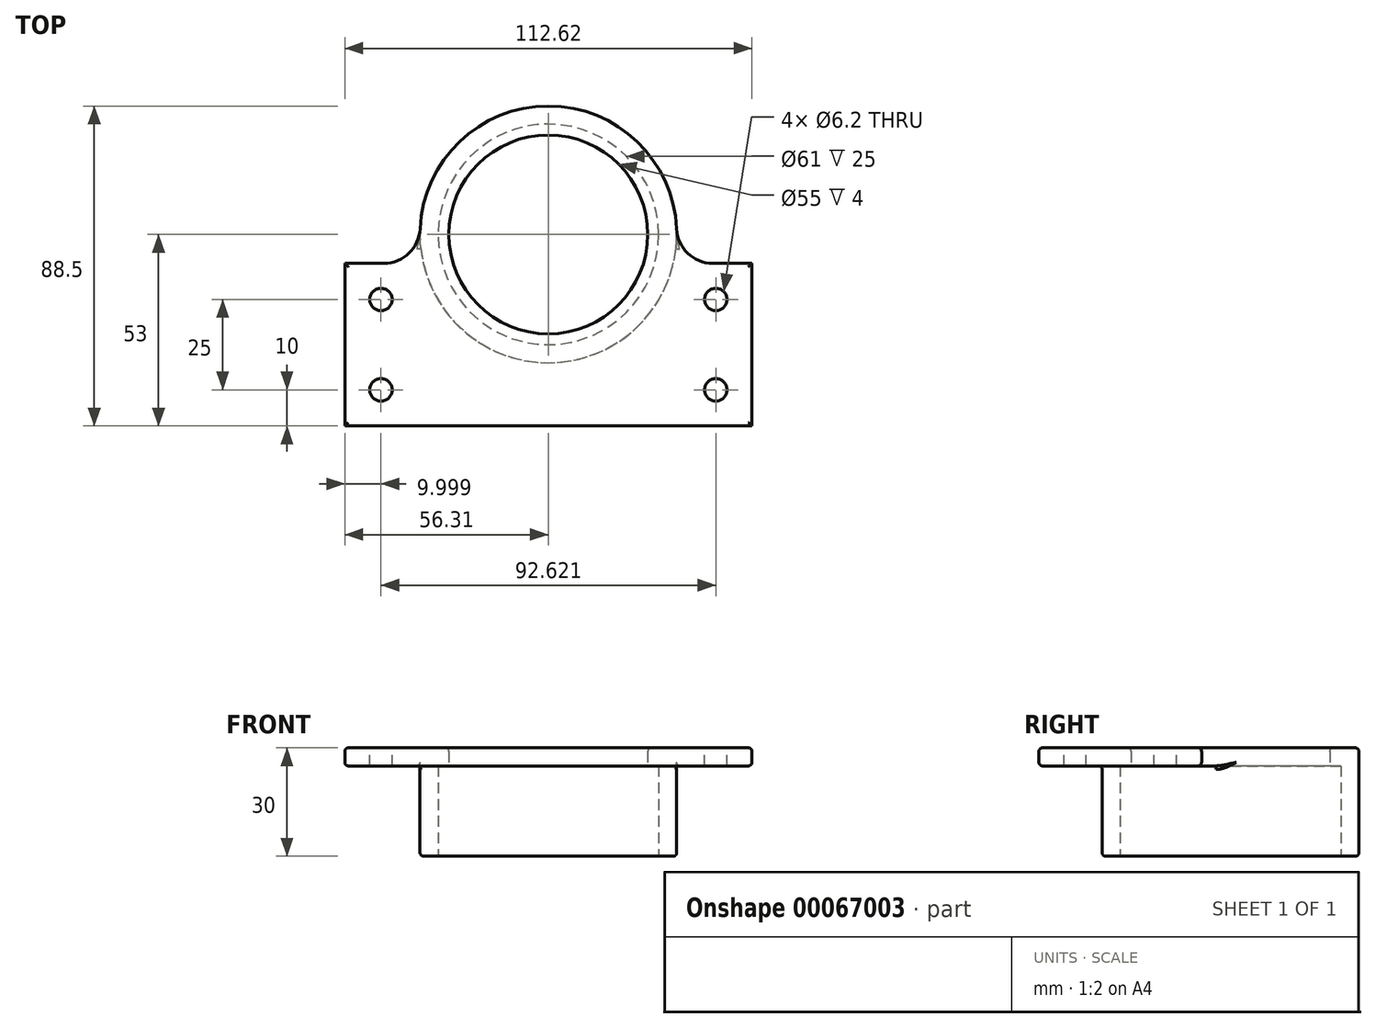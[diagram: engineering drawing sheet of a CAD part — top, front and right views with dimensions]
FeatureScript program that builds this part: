
annotation { "Feature Type Name" : "Feature", "Feature Type Description" : "" }
export const myFeature = defineFeature(function(context is Context, id is Id, definition is map)
    precondition{}
    {
        {
            var Q0;
            Q0=qCreatedBy(makeId("Top.planeOp"),FACE);
            var sketch = newSketch(context, id + "F0", { "sketchPlane" : qUnion([Q0])});
            skCircle(sketch, "E0", {"center": v(-19.8, 0.63) * mm, "radius": 3.1 * mm, "construction": true});
            skCircle(sketch, "E1", {"center": v(19.8, 0.63) * mm, "radius": 3.1 * mm, "construction": true});
            skLineSegment(sketch, "E2", {"start": v(-19.8, 0.63) * mm, "end": v(19.8, 0.63) * mm, "construction": true});
            skCircle(sketch, "E3", {"center": v(0, 0) * mm, "radius": 30.5 * mm});
            skCircle(sketch, "E4", {"center": v(0, 0) * mm, "radius": 35.5 * mm});
            skSolve(sketch);
        }
        {
            var Q0;
            Q0 = qSketchRegion(id + "F0", true);
            extrude(context, id + "F1", {"entities" : qUnion([Q0]), "depth" : 25 * mm});
        }
        {
            var Q0;
            Q0=makeQuery(id+"F1.opExtrude","CAP_FACE",FACE,{"disambiguationData":[OSD([sQuery(id+"F0.wireOp",EDGE,"E3"),sQuery(id+"F0.wireOp",EDGE,"E4")])],"isStart":false});
            var sketch = newSketch(context, id + "F2", { "sketchPlane" : qUnion([Q0])});
            skCircle(sketch, "E5", {"center": v(0, 0) * mm, "radius": 27.5 * mm});
            skCircle(sketch, "E6", {"center": v(0, 0) * mm, "radius": 35.5 * mm});
            skSolve(sketch);
        }
        {
            var Q0;
            Q0 = qSketchRegion(id + "F2", true);
            extrude(context, id + "F3", {"entities" : qUnion([Q0]), "operationType" : NewBodyOperationType.ADD, "depth" : 5 * mm});
        }
        {
            var Q0;
            Q0=makeQuery(id+"F3.opExtrude","CAP_FACE",FACE,{"disambiguationData":[OSD([sQuery(id+"F2.wireOp",EDGE,"E5"),sQuery(id+"F2.wireOp",EDGE,"E6")])],"isStart":false});
            var sketch = newSketch(context, id + "F4", { "sketchPlane" : qUnion([Q0])});
            skLineSegment(sketch, "E7", {"start": v(-26.31, -8) * mm, "end": v(-56.31, -8) * mm});
            skLineSegment(sketch, "E8", {"start": v(-56.31, -8) * mm, "end": v(-56.31, -53) * mm});
            skLineSegment(sketch, "E9", {"start": v(-56.31, -53) * mm, "end": v(56.31, -53) * mm});
            skLineSegment(sketch, "E10", {"start": v(56.31, -53) * mm, "end": v(56.31, -8) * mm});
            skLineSegment(sketch, "E11", {"start": v(56.31, -8) * mm, "end": v(26.31, -8) * mm});
            skArc(sketch, "E12", {"start": v(26.31, -8) * mm, "mid": v(0, -27.5) * mm, "end": v(-26.31, -8) * mm});
            skSolve(sketch);
        }
        {
            var Q0;
            Q0 = qSketchRegion(id + "F4", true);
            extrude(context, id + "F5", {"entities" : qUnion([Q0]), "operationType" : NewBodyOperationType.ADD, "oppositeDirection" : true, "depth" : 5 * mm});
        }
        {
            var Q0;
            Q0=makeQuery(id+"F5.boolean.opBoolean","INTERSECT",EDGE,{"derivedFrom":[makeQuery(id+"F3.boolean.opBoolean","MERGE",FACE,{"derivedFrom":[makeQuery(id+"F1.opExtrude","SWEPT_FACE",FACE,{"disambiguationData":[OSD([sQuery(id+"F0.wireOp",EDGE,"E4")])]}),makeQuery(id+"F3.opExtrude","SWEPT_FACE",FACE,{"disambiguationData":[OSD([sQuery(id+"F2.wireOp",EDGE,"E6")])]})]}),makeQuery(id+"F5.opExtrude","SWEPT_FACE",FACE,{"disambiguationData":[OSD([sQuery(id+"F4.wireOp",EDGE,"E11")])]})]});
            var Q1;
            Q1=makeQuery(id+"F5.boolean.opBoolean","INTERSECT",EDGE,{"derivedFrom":[makeQuery(id+"F3.boolean.opBoolean","MERGE",FACE,{"derivedFrom":[makeQuery(id+"F1.opExtrude","SWEPT_FACE",FACE,{"disambiguationData":[OSD([sQuery(id+"F0.wireOp",EDGE,"E4")])]}),makeQuery(id+"F3.opExtrude","SWEPT_FACE",FACE,{"disambiguationData":[OSD([sQuery(id+"F2.wireOp",EDGE,"E6")])]})]}),makeQuery(id+"F5.opExtrude","SWEPT_FACE",FACE,{"disambiguationData":[OSD([sQuery(id+"F4.wireOp",EDGE,"E7")])]})]});
            fillet(context, id + "F6", {"entities" : qUnion([Q0, Q1]), "radius" : 10 * mm, "tangentPropagation" : true, "allowEdgeOverflow" : false});
        }
        {
            var Q0;
            Q0=makeQuery(id+"F5.boolean.opBoolean","MERGE",FACE,{"derivedFrom":[makeQuery(id+"F3.opExtrude","CAP_FACE",FACE,{"disambiguationData":[OSD([sQuery(id+"F2.wireOp",EDGE,"E5"),sQuery(id+"F2.wireOp",EDGE,"E6")])],"isStart":false}),makeQuery(id+"F5.opExtrude","CAP_FACE",FACE,{"disambiguationData":[OSD([sQuery(id+"F4.wireOp",EDGE,"E7"),sQuery(id+"F4.wireOp",EDGE,"E8"),sQuery(id+"F4.wireOp",EDGE,"E9"),sQuery(id+"F4.wireOp",EDGE,"E10"),sQuery(id+"F4.wireOp",EDGE,"E11"),sQuery(id+"F4.wireOp",EDGE,"E12")])],"isStart":true})]});
            var Q1;
            Q1=makeQuery(id+"F1.opExtrude","CAP_EDGE",EDGE,{"disambiguationData":[OSD([sQuery(id+"F0.wireOp",EDGE,"E4")])],"isStart":true});
            var Q2;
            Q2=makeQuery(id+"F5.opExtrude","CAP_FACE",FACE,{"disambiguationData":[OSD([sQuery(id+"F4.wireOp",EDGE,"E7"),sQuery(id+"F4.wireOp",EDGE,"E8"),sQuery(id+"F4.wireOp",EDGE,"E9"),sQuery(id+"F4.wireOp",EDGE,"E10"),sQuery(id+"F4.wireOp",EDGE,"E11"),sQuery(id+"F4.wireOp",EDGE,"E12")])],"isStart":false});
            fillet(context, id + "F7", {"entities" : qUnion([Q0, Q1, Q2]), "radius" : 1 * mm, "tangentPropagation" : true, "allowEdgeOverflow" : false});
        }
        {
            var Q0;
            Q0=makeQuery(id+"F5.boolean.opBoolean","MERGE",FACE,{"derivedFrom":[makeQuery(id+"F3.opExtrude","CAP_FACE",FACE,{"disambiguationData":[OSD([sQuery(id+"F2.wireOp",EDGE,"E5"),sQuery(id+"F2.wireOp",EDGE,"E6")])],"isStart":false}),makeQuery(id+"F5.opExtrude","CAP_FACE",FACE,{"disambiguationData":[OSD([sQuery(id+"F4.wireOp",EDGE,"E7"),sQuery(id+"F4.wireOp",EDGE,"E8"),sQuery(id+"F4.wireOp",EDGE,"E9"),sQuery(id+"F4.wireOp",EDGE,"E10"),sQuery(id+"F4.wireOp",EDGE,"E11"),sQuery(id+"F4.wireOp",EDGE,"E12")])],"isStart":true})]});
            var sketch = newSketch(context, id + "F8", { "sketchPlane" : qUnion([Q0])});
            skCircle(sketch, "E13", {"center": v(-46.31, -18) * mm, "radius": 3.1 * mm});
            skCircle(sketch, "E14", {"center": v(-46.31, -43) * mm, "radius": 3.1 * mm});
            skCircle(sketch, "E15", {"center": v(46.31, -18) * mm, "radius": 3.1 * mm});
            skCircle(sketch, "E16", {"center": v(46.31, -43) * mm, "radius": 3.1 * mm});
            skSolve(sketch);
        }
        {
            var Q0;
            Q0 = qSketchRegion(id + "F8", true);
            extrude(context, id + "F9", {"entities" : qUnion([Q0]), "operationType" : NewBodyOperationType.REMOVE, "endBound" : BoundingType.THROUGH_ALL, "oppositeDirection" : true, "depth" : 25 * mm});
        }
    });
